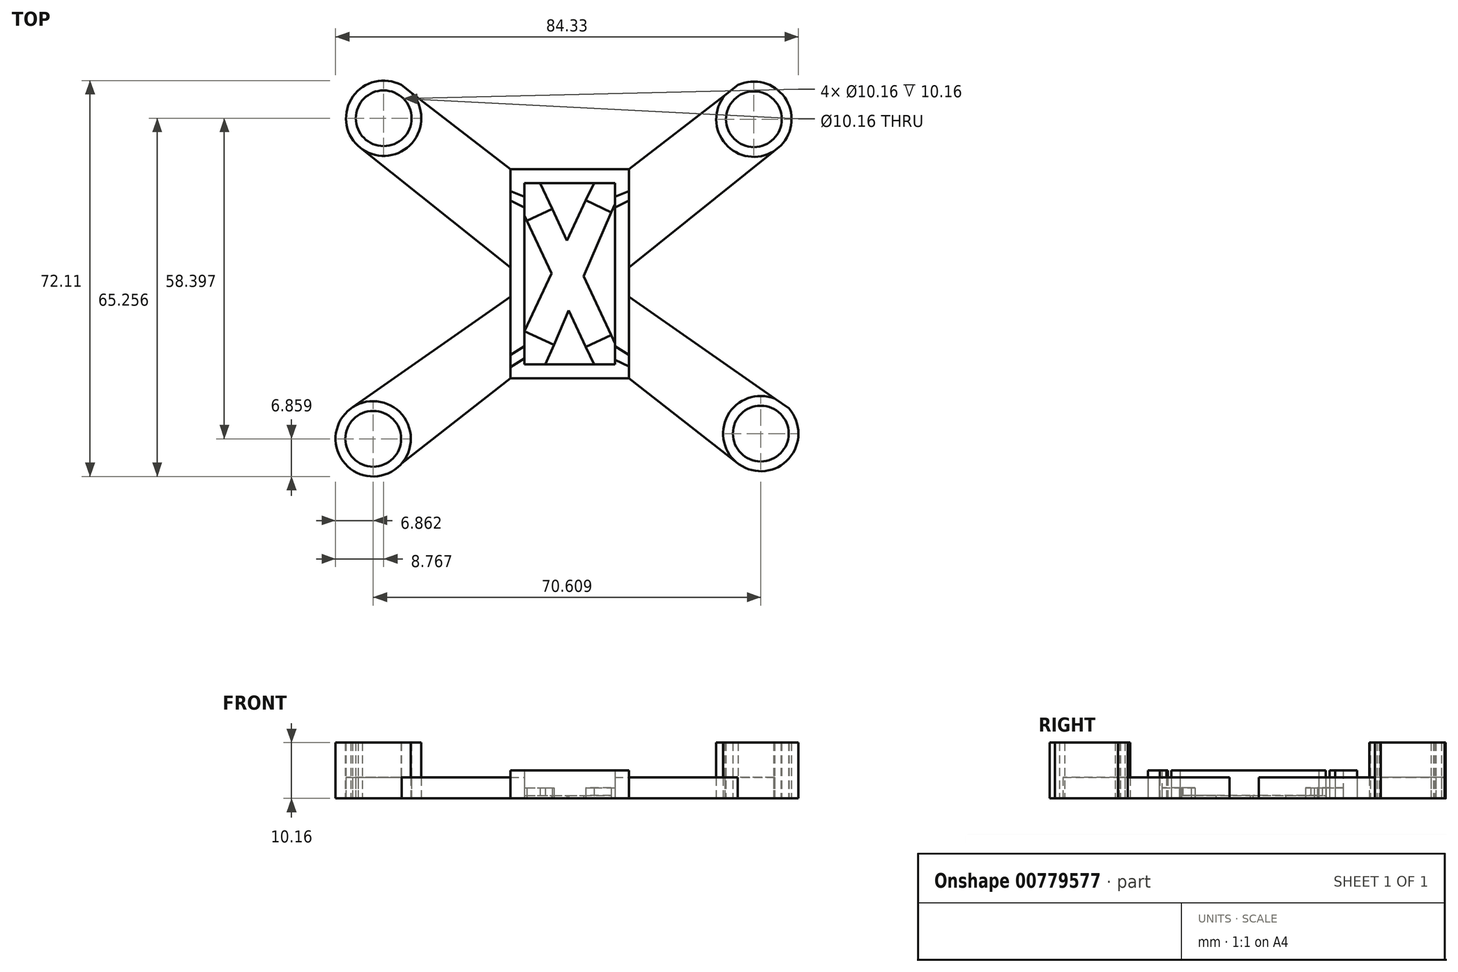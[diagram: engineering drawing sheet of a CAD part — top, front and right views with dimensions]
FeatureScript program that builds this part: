
annotation { "Feature Type Name" : "Feature", "Feature Type Description" : "" }
export const myFeature = defineFeature(function(context is Context, id is Id, definition is map)
    precondition{}
    {
        {
            var Q0;
            Q0=qCreatedBy(makeId("Top.planeOp"),FACE);
            var sketch = newSketch(context, id + "F0", { "sketchPlane" : qUnion([Q0])});
            skLineSegment(sketch, "E0.bottom", {"start": v(3.61, 10.7) * mm, "end": v(20.07, 10.7) * mm});
            skLineSegment(sketch, "E0.top", {"start": v(3.61, 43.72) * mm, "end": v(20.07, 43.72) * mm});
            skLineSegment(sketch, "E0.left", {"start": v(3.61, 10.7) * mm, "end": v(3.61, 43.72) * mm});
            skLineSegment(sketch, "E0.right", {"start": v(20.07, 10.7) * mm, "end": v(20.07, 43.72) * mm});
            skLineSegment(sketch, "E1", {"start": v(7.42, 10.7) * mm, "end": v(11.68, 20.54) * mm});
            skLineSegment(sketch, "E2", {"start": v(3.61, 16.75) * mm, "end": v(8.54, 27.26) * mm});
            skLineSegment(sketch, "E3", {"start": v(19.43, 38.42) * mm, "end": v(14.8, 40.59) * mm});
            skLineSegment(sketch, "E4.0", {"start": v(1.07, 8.17) * mm, "end": v(22.61, 8.17) * mm});
            skLineSegment(sketch, "E4.1", {"start": v(1.07, 8.17) * mm, "end": v(1.07, 46.26) * mm});
            skLineSegment(sketch, "E4.2", {"start": v(1.07, 46.26) * mm, "end": v(22.61, 46.26) * mm});
            skLineSegment(sketch, "E4.3", {"start": v(22.61, 8.17) * mm, "end": v(22.61, 46.26) * mm});
            skLineSegment(sketch, "E5.trimOffspring", {"start": v(14.37, 26.75) * mm, "end": v(20.07, 39.91) * mm});
            skLineSegment(sketch, "E6.trimOffspring", {"start": v(11.35, 33.24) * mm, "end": v(16.26, 43.72) * mm});
            skCircle(sketch, "E7", {"center": v(-23.96, -2.86) * mm, "radius": 5.08 * mm});
            skCircle(sketch, "E8", {"center": v(46.65, -1.9) * mm, "radius": 5.08 * mm});
            skCircle(sketch, "E9", {"center": v(-22.05, 55.54) * mm, "radius": 5.08 * mm});
            skCircle(sketch, "E10", {"center": v(45.4, 55.37) * mm, "radius": 5.08 * mm});
            skLineSegment(sketch, "E11", {"start": v(3.61, 16.75) * mm, "end": v(8.96, 14.25) * mm});
            skLineSegment(sketch, "E12", {"start": v(3.61, 37.84) * mm, "end": v(8.54, 27.26) * mm});
            skLineSegment(sketch, "E13", {"start": v(6.46, 43.72) * mm, "end": v(11.35, 33.24) * mm});
            skLineSegment(sketch, "E14", {"start": v(4.06, 36.88) * mm, "end": v(8.65, 39.02) * mm});
            skLineSegment(sketch, "E15", {"start": v(19.37, 16.03) * mm, "end": v(14.78, 13.89) * mm});
            skLineSegment(sketch, "E16.trimOffspring", {"start": v(11.68, 20.54) * mm, "end": v(16.26, 10.7) * mm});
            skLineSegment(sketch, "E17.trimOffspring", {"start": v(14.37, 26.75) * mm, "end": v(20.07, 14.52) * mm});
            skLineSegment(sketch, "E18", {"start": v(1.07, 10.21) * mm, "end": v(3.61, 11.77) * mm});
            skLineSegment(sketch, "E19", {"start": v(1.07, 12.43) * mm, "end": v(3.61, 14) * mm});
            skLineSegment(sketch, "E20", {"start": v(1.07, 40.54) * mm, "end": v(3.61, 39.3) * mm});
            skLineSegment(sketch, "E21", {"start": v(1.07, 42.23) * mm, "end": v(3.61, 41.25) * mm});
            skLineSegment(sketch, "E22.MirrorCS", {"start": v(22.61, 40.54) * mm, "end": v(20.07, 39.3) * mm});
            skLineSegment(sketch, "E23.MirrorCS", {"start": v(22.61, 42.23) * mm, "end": v(20.07, 41.25) * mm});
            skLineSegment(sketch, "E24.MirrorCS", {"start": v(22.61, 12.43) * mm, "end": v(20.07, 14) * mm});
            skCircle(sketch, "E25", {"center": v(-22.05, 55.54) * mm, "radius": 6.86 * mm});
            skCircle(sketch, "E26", {"center": v(45.4, 55.37) * mm, "radius": 6.86 * mm});
            skCircle(sketch, "E27", {"center": v(-23.96, -2.86) * mm, "radius": 6.86 * mm});
            skCircle(sketch, "E28", {"center": v(46.65, -1.9) * mm, "radius": 6.86 * mm});
            skLineSegment(sketch, "E29", {"start": v(-18.85, 61.6) * mm, "end": v(1.07, 46.26) * mm});
            skLineSegment(sketch, "E30", {"start": v(-26.72, 50.5) * mm, "end": v(1.07, 28.32) * mm});
            skLineSegment(sketch, "E31", {"start": v(42.54, 61.6) * mm, "end": v(22.61, 46.26) * mm});
            skLineSegment(sketch, "E32", {"start": v(50.33, 50.6) * mm, "end": v(22.61, 28.33) * mm});
            skLineSegment(sketch, "E33", {"start": v(22.61, 8.17) * mm, "end": v(42.43, -7.31) * mm});
            skLineSegment(sketch, "E34", {"start": v(51.76, 2.67) * mm, "end": v(22.61, 23.05) * mm});
            skLineSegment(sketch, "E35", {"start": v(-18.74, -7.31) * mm, "end": v(1.07, 8.17) * mm});
            skLineSegment(sketch, "E36", {"start": v(-28.05, 2.64) * mm, "end": v(1.07, 23.04) * mm});
            skLineSegment(sketch, "E37", {"start": v(20.07, 11.52) * mm, "end": v(22.61, 10.33) * mm});
            skSolve(sketch);
        }
        {
            var Q0;
            {var subQ5=sQuery(id+"F0.wireOp",EDGE,"U1ISGbGf-jrig-8iwu-J9oZ-XZOoRxxGoM5B");Q0=makeQuery(id+"F0.imprint","IMPRINT",FACE,{"disambiguationData":[TD([[makeQuery(id+"F0.imprint","IMPRINT",EDGE,{"derivedFrom":subQ5}),1.0]])]});}
            var Q1;
            {var subQ1=sQuery(id+"F0.wireOp",EDGE,"E3");Q1=makeQuery(id+"F0.imprint","IMPRINT",FACE,{"disambiguationData":[TD([[makeQuery(id+"F0.imprint","IMPRINT",EDGE,{"derivedFrom":subQ1}),-1.0]])]});}
            var Q2;
            {var subQ5=sQuery(id+"F0.wireOp",EDGE,"E11");Q2=makeQuery(id+"F0.imprint","IMPRINT",FACE,{"disambiguationData":[TD([[makeQuery(id+"F0.imprint","IMPRINT",EDGE,{"derivedFrom":subQ5}),-1.0]])]});}
            var Q3;
            {var subQ5=sQuery(id+"F0.wireOp",EDGE,"zNn4E79E-JaBV-f59J-6CTJ-gznBW4pIjXGX");Q3=makeQuery(id+"F0.imprint","IMPRINT",FACE,{"disambiguationData":[TD([[makeQuery(id+"F0.imprint","IMPRINT",EDGE,{"derivedFrom":subQ5}),-1.0]])]});}
            var Q4;
            {var subQ0=sQuery(id+"F0.wireOp",EDGE,"E15");Q4=makeQuery(id+"F0.imprint","IMPRINT",FACE,{"disambiguationData":[TD([[makeQuery(id+"F0.imprint","IMPRINT",EDGE,{"derivedFrom":subQ0}),1.0]])]});}
            var Q5;
            {var subQ3=sQuery(id+"F0.wireOp",EDGE,"E14");Q5=makeQuery(id+"F0.imprint","IMPRINT",FACE,{"disambiguationData":[TD([[makeQuery(id+"F0.imprint","IMPRINT",EDGE,{"derivedFrom":subQ3}),1.0]])]});}
            extrude(context, id + "F1", {"entities" : qUnion([Q0, Q1, Q2, Q3, Q4, Q5]), "depth" : 1.9 * mm, "offsetDistance" : 25.4 * mm});
        }
        {
            var Q0;
            {var subQ2=sQuery(id+"F0.wireOp",EDGE,"E2");Q0=makeQuery(id+"F0.imprint","IMPRINT",FACE,{"disambiguationData":[TD([[makeQuery(id+"F0.imprint","IMPRINT",EDGE,{"derivedFrom":subQ2}),-1.0]])]});}
            extrude(context, id + "F2", {"entities" : qUnion([Q0]), "depth" : 0.5 * mm, "offsetDistance" : 25.4 * mm});
        }
        {
            var Q0;
            {var subQ3=sQuery(id+"F0.wireOp",EDGE,"Lp0lejn1-J9I6-99vP-2keL-ePVxwC7CkpDk");Q0=makeQuery(id+"F0.imprint","IMPRINT",FACE,{"disambiguationData":[TD([[makeQuery(id+"F0.imprint","IMPRINT",EDGE,{"derivedFrom":subQ3}),1.0]])]});}
            var Q1;
            {var subQ4=sQuery(id+"F0.wireOp",EDGE,"E4.2");Q1=makeQuery(id+"F0.imprint","IMPRINT",FACE,{"disambiguationData":[TD([[makeQuery(id+"F0.imprint","IMPRINT",EDGE,{"derivedFrom":subQ4}),-1.0]])]});}
            var Q2;
            {var subQ6=sQuery(id+"F0.wireOp",EDGE,"GEmbjNxS-5cSQ-f9E5-M6BZ-vidzlD44SodT");Q2=makeQuery(id+"F0.imprint","IMPRINT",FACE,{"disambiguationData":[TD([[makeQuery(id+"F0.imprint","IMPRINT",EDGE,{"derivedFrom":subQ6}),1.0]])]});}
            var Q3;
            {var subQ3=sQuery(id+"F0.wireOp",EDGE,"Z0jz2gNn-EpKk-Zu0g-wZnS-NRbnvPRwyOgk");Q3=makeQuery(id+"F0.imprint","IMPRINT",FACE,{"disambiguationData":[TD([[makeQuery(id+"F0.imprint","IMPRINT",EDGE,{"derivedFrom":subQ3}),-1.0]])]});}
            var Q4;
            {var subQ2=sQuery(id+"F0.wireOp",EDGE,"E19");Q4=makeQuery(id+"F0.imprint","IMPRINT",FACE,{"disambiguationData":[TD([[makeQuery(id+"F0.imprint","IMPRINT",EDGE,{"derivedFrom":subQ2}),1.0]])]});}
            var Q5;
            {var subQ5=sQuery(id+"F0.wireOp",EDGE,"E22.MirrorCS");Q5=makeQuery(id+"F0.imprint","IMPRINT",FACE,{"disambiguationData":[TD([[makeQuery(id+"F0.imprint","IMPRINT",EDGE,{"derivedFrom":subQ5}),1.0]])]});}
            var Q6;
            {var subQ6=sQuery(id+"F0.wireOp",EDGE,"E4.0");Q6=makeQuery(id+"F0.imprint","IMPRINT",FACE,{"disambiguationData":[TD([[makeQuery(id+"F0.imprint","IMPRINT",EDGE,{"derivedFrom":subQ6}),1.0]])]});}
            extrude(context, id + "F3", {"entities" : qUnion([Q0, Q1, Q2, Q3, Q4, Q5, Q6]), "depth" : 5.08 * mm, "offsetDistance" : 25.4 * mm});
        }
        {
            var Q0;
            {var subQ0=sQuery(id+"F0.wireOp",EDGE,"1NyYy8js-mDI4-lnA9-UoNe-qzddwHOFsHQd");Q0=makeQuery(id+"F0.imprint","IMPRINT",FACE,{"disambiguationData":[TD([[makeQuery(id+"F0.imprint","IMPRINT",EDGE,{"derivedFrom":subQ0}),-1.0]])]});}
            var Q1;
            {var subQ0=sQuery(id+"F0.wireOp",EDGE,"91U7G9ms-mkzw-ZKWX-5uum-9Az9oErxjuHQ");Q1=makeQuery(id+"F0.imprint","IMPRINT",FACE,{"disambiguationData":[TD([[makeQuery(id+"F0.imprint","IMPRINT",EDGE,{"derivedFrom":subQ0}),-1.0]])]});}
            var Q2;
            {var subQ4=sQuery(id+"F0.wireOp",EDGE,"VwybiR1R-IEba-ExoY-xV1U-KTpVhCcxKk0u");Q2=makeQuery(id+"F0.imprint","IMPRINT",FACE,{"disambiguationData":[TD([[makeQuery(id+"F0.imprint","IMPRINT",EDGE,{"derivedFrom":subQ4}),1.0]])]});}
            var Q3;
            {var subQ3=sQuery(id+"F0.wireOp",EDGE,"XlycJJHm-YZ2H-1SAr-YmSB-kWeGzfCjxfBY");Q3=makeQuery(id+"F0.imprint","IMPRINT",FACE,{"disambiguationData":[TD([[makeQuery(id+"F0.imprint","IMPRINT",EDGE,{"derivedFrom":subQ3}),1.0]])]});}
            var Q4;
            {var subQ4=sQuery(id+"F0.wireOp",EDGE,"obwRu7iz-BBBC-3NCY-CqlE-6dwO7JDknqMH");Q4=makeQuery(id+"F0.imprint","IMPRINT",FACE,{"disambiguationData":[TD([[makeQuery(id+"F0.imprint","IMPRINT",EDGE,{"derivedFrom":subQ4}),1.0]])]});}
            var Q5;
            {var subQ4=sQuery(id+"F0.wireOp",EDGE,"Wx7L9XRe-BvjI-BGih-pwvk-7DQ00SZ51gZ3");Q5=makeQuery(id+"F0.imprint","IMPRINT",FACE,{"disambiguationData":[TD([[makeQuery(id+"F0.imprint","IMPRINT",EDGE,{"derivedFrom":subQ4}),1.0]])]});}
            var Q6;
            {var subQ4=sQuery(id+"F0.wireOp",EDGE,"TOs8OfCI-VQA3-iajt-2VeR-PiLy7yfJ2J0x");Q6=makeQuery(id+"F0.imprint","IMPRINT",FACE,{"disambiguationData":[TD([[makeQuery(id+"F0.imprint","IMPRINT",EDGE,{"derivedFrom":subQ4}),1.0]])]});}
            var Q7;
            {var subQ0=sQuery(id+"F0.wireOp",EDGE,"RAxnpRw0-KfuO-2YTs-QPmg-lOcG9lFrW7Uz");Q7=makeQuery(id+"F0.imprint","IMPRINT",FACE,{"disambiguationData":[TD([[makeQuery(id+"F0.imprint","IMPRINT",EDGE,{"derivedFrom":subQ0}),-1.0]])]});}
            var Q8;
            Q8=makeQuery(id+"F0.imprint","IMPRINT",FACE,{"disambiguationData":[TD([[makeQuery(id+"F0.imprint","IMPRINT",EDGE,{"derivedFrom":sQuery(id+"F0.wireOp",EDGE,"E10")}),-1.0]])]});
            var Q9;
            Q9=makeQuery(id+"F0.imprint","IMPRINT",FACE,{"disambiguationData":[TD([[makeQuery(id+"F0.imprint","IMPRINT",EDGE,{"derivedFrom":sQuery(id+"F0.wireOp",EDGE,"E9")}),-1.0]])]});
            var Q10;
            Q10=makeQuery(id+"F0.imprint","IMPRINT",FACE,{"disambiguationData":[TD([[makeQuery(id+"F0.imprint","IMPRINT",EDGE,{"derivedFrom":sQuery(id+"F0.wireOp",EDGE,"E7")}),-1.0]])]});
            var Q11;
            Q11=makeQuery(id+"F0.imprint","IMPRINT",FACE,{"disambiguationData":[TD([[makeQuery(id+"F0.imprint","IMPRINT",EDGE,{"derivedFrom":sQuery(id+"F0.wireOp",EDGE,"E8")}),-1.0]])]});
            extrude(context, id + "F4", {"entities" : qUnion([Q0, Q1, Q2, Q3, Q4, Q5, Q6, Q7, Q8, Q9, Q10, Q11]), "depth" : 10.16 * mm, "offsetDistance" : 25.4 * mm});
        }
        {
            var Q0;
            {var subQ0=sQuery(id+"F0.wireOp",EDGE,"x9NTftKn-Bqew-1Nt0-5X5N-tuHgA9GR64zg");Q0=makeQuery(id+"F0.imprint","IMPRINT",FACE,{"disambiguationData":[TD([[makeQuery(id+"F0.imprint","IMPRINT",EDGE,{"derivedFrom":subQ0}),-1.0]])]});}
            var Q1;
            {var subQ0=sQuery(id+"F0.wireOp",EDGE,"RmOsVucf-aK7b-AnJ8-Obm7-94f16jtztpDg");var subQ5=sQuery(id+"F0.wireOp",EDGE,"E9");var subQ6=makeQuery(id+"F0.imprint","INTERSECT",VERTEX,{"disambiguationData":[OD(1.0)],"derivedFrom":[subQ5,subQ0]});Q1=makeQuery(id+"F0.imprint","IMPRINT",FACE,{"disambiguationData":[TD([[makeQuery(id+"F0.imprint","IMPRINT",EDGE,{"disambiguationData":[TD([[subQ6,1.0]])],"derivedFrom":subQ5}),-1.0]])]});}
            var Q2;
            {var subQ2=sQuery(id+"F0.wireOp",EDGE,"2Wmyqjzu-PTuz-MBIS-31le-kWs6nasyH1p7");Q2=makeQuery(id+"F0.imprint","IMPRINT",FACE,{"disambiguationData":[TD([[makeQuery(id+"F0.imprint","IMPRINT",EDGE,{"derivedFrom":subQ2}),1.0]])]});}
            var Q3;
            {var subQ0=sQuery(id+"F0.wireOp",EDGE,"SK2cpyIQ-Yu2f-mXYX-hFqe-vlb6NJ34hbxP");Q3=makeQuery(id+"F0.imprint","IMPRINT",FACE,{"disambiguationData":[TD([[makeQuery(id+"F0.imprint","IMPRINT",EDGE,{"derivedFrom":subQ0}),1.0]])]});}
            var Q4;
            {var subQ0=sQuery(id+"F0.wireOp",EDGE,"HPRsAgNH-ikqN-j3M2-eJVg-DJldIqc8Aj9K");Q4=makeQuery(id+"F0.imprint","IMPRINT",FACE,{"disambiguationData":[TD([[makeQuery(id+"F0.imprint","IMPRINT",EDGE,{"derivedFrom":subQ0}),-1.0]])]});}
            var Q5;
            {var subQ0=sQuery(id+"F0.wireOp",EDGE,"C1usgjXu-KLwX-s6qm-zQ80-SANBLfo8HFCN");Q5=makeQuery(id+"F0.imprint","IMPRINT",FACE,{"disambiguationData":[TD([[makeQuery(id+"F0.imprint","IMPRINT",EDGE,{"derivedFrom":subQ0}),1.0]])]});}
            var Q6;
            {var subQ7=sQuery(id+"F0.wireOp",EDGE,"E33");Q6=makeQuery(id+"F0.imprint","IMPRINT",FACE,{"disambiguationData":[TD([[makeQuery(id+"F0.imprint","IMPRINT",EDGE,{"derivedFrom":subQ7}),1.0]])]});}
            var Q7;
            {var subQ5=sQuery(id+"F0.wireOp",EDGE,"E4.3");var subQ6=makeQuery(id+"F0.imprint","INTERSECT",VERTEX,{"derivedFrom":[subQ5,sQuery(id+"F0.wireOp",EDGE,"E22.MirrorCS")]});Q7=makeQuery(id+"F0.imprint","IMPRINT",FACE,{"disambiguationData":[TD([[makeQuery(id+"F0.imprint","IMPRINT",EDGE,{"disambiguationData":[TD([[subQ6,1.0]])],"derivedFrom":subQ5}),-1.0]])]});}
            var Q8;
            {var subQ6=sQuery(id+"F0.wireOp",EDGE,"E35");Q8=makeQuery(id+"F0.imprint","IMPRINT",FACE,{"disambiguationData":[TD([[makeQuery(id+"F0.imprint","IMPRINT",EDGE,{"derivedFrom":subQ6}),1.0]])]});}
            var Q9;
            {var subQ1=sQuery(id+"F0.wireOp",EDGE,"E4.1");var subQ4=makeQuery(id+"F0.imprint","INTERSECT",VERTEX,{"derivedFrom":[subQ1,sQuery(id+"F0.wireOp",EDGE,"E20")]});Q9=makeQuery(id+"F0.imprint","IMPRINT",FACE,{"disambiguationData":[TD([[makeQuery(id+"F0.imprint","IMPRINT",EDGE,{"disambiguationData":[TD([[subQ4,1.0]])],"derivedFrom":subQ1}),1.0]])]});}
            extrude(context, id + "F5", {"entities" : qUnion([Q0, Q1, Q2, Q3, Q4, Q5, Q6, Q7, Q8, Q9]), "depth" : 3.8 * mm, "offsetDistance" : 25.4 * mm});
        }
        {
            var Q0;
            {var subQ0=sQuery(id+"F0.wireOp",EDGE,"E20");Q0=makeQuery(id+"F0.imprint","IMPRINT",FACE,{"disambiguationData":[TD([[makeQuery(id+"F0.imprint","IMPRINT",EDGE,{"derivedFrom":subQ0}),1.0]])]});}
            var Q1;
            {var subQ0=sQuery(id+"F0.wireOp",EDGE,"E22.MirrorCS");Q1=makeQuery(id+"F0.imprint","IMPRINT",FACE,{"disambiguationData":[TD([[makeQuery(id+"F0.imprint","IMPRINT",EDGE,{"derivedFrom":subQ0}),-1.0]])]});}
            var Q2;
            {var subQ0=sQuery(id+"F0.wireOp",EDGE,"7e91d56d-224b-49fc-9e4c-d535d7cd5fcb0.MirrorCS");Q2=makeQuery(id+"F0.imprint","IMPRINT",FACE,{"disambiguationData":[TD([[makeQuery(id+"F0.imprint","IMPRINT",EDGE,{"derivedFrom":subQ0}),-1.0]])]});}
            var Q3;
            {var subQ0=sQuery(id+"F0.wireOp",EDGE,"E18");Q3=makeQuery(id+"F0.imprint","IMPRINT",FACE,{"disambiguationData":[TD([[makeQuery(id+"F0.imprint","IMPRINT",EDGE,{"derivedFrom":subQ0}),1.0]])]});}
            var Q4;
            {var subQ0=sQuery(id+"F0.wireOp",EDGE,"E24.MirrorCS");Q4=makeQuery(id+"F0.imprint","IMPRINT",FACE,{"disambiguationData":[TD([[makeQuery(id+"F0.imprint","IMPRINT",EDGE,{"derivedFrom":subQ0}),1.0]])]});}
            extrude(context, id + "F6", {"entities" : qUnion([Q0, Q1, Q2, Q3, Q4]), "depth" : 3.8 * mm, "offsetDistance" : 25.4 * mm});
        }
    });
